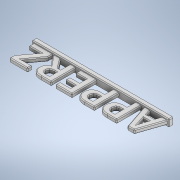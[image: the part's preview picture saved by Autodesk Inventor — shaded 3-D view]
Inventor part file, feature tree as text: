
AUTODESK INVENTOR PART (.ipt)
format: ipt  version: 2020 (Build 240168000, 168)  size: 651,264 bytes
history: native  units: in
note: dims shown in document units (in); Inventor stores cm internally (conversion verified against a paired STEP export)
features: extrude x2, chamfer x2, sketch x2
ambient origin geometry x8: Origin, YZ Plane, XZ Plane, XY Plane, X Axis, Y Axis, Z Axis, Center Point
bodies: Solid1 (feature_tree)
feature tree (6):
  extrude  "Extrusion1"  Depth=0.0787in
  extrude  "Extrusion2"  Depth=0.0787in
  chamfer  "Chamfer1"  Distance=0.0787in
  chamfer  "Chamfer2"  Distance=0.1969in
  sketch  "Sketch1"  dims[d0=0.1969in d1=0.0in d2=0.0787in]
  sketch  "Sketch2"  dims[d3=0.0787in d4=0.0787in d5=0.0787in d6=0.1969in d7=0.0in d8=0.0394in d9=0.125in d10=45.0deg d11=0.0394in d12=0.125in d13=45.0deg]
